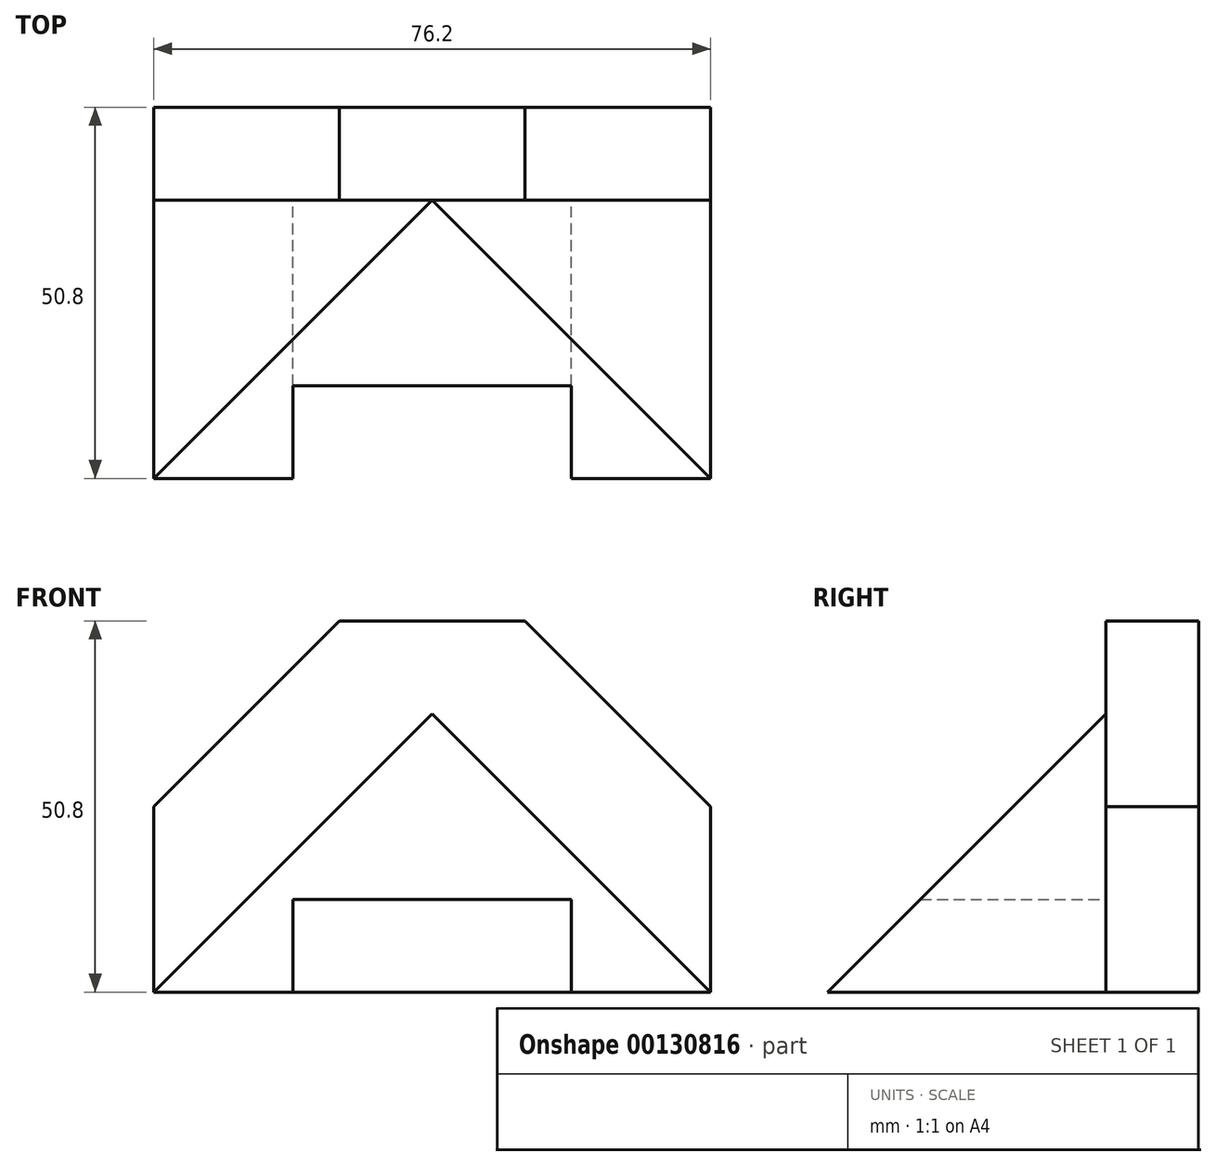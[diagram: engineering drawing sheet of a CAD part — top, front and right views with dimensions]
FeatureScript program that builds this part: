
annotation { "Feature Type Name" : "Feature", "Feature Type Description" : "" }
export const myFeature = defineFeature(function(context is Context, id is Id, definition is map)
    precondition{}
    {
        {
            var Q0;
            Q0=qCreatedBy(makeId("Top.planeOp"),FACE);
            var sketch = newSketch(context, id + "F0", { "sketchPlane" : qUnion([Q0])});
            skLineSegment(sketch, "E0", {"start": v(0, 0) * mm, "end": v(0, 50.8) * mm});
            skLineSegment(sketch, "E1", {"start": v(0, 50.8) * mm, "end": v(76.2, 50.8) * mm});
            skLineSegment(sketch, "E2", {"start": v(76.2, 50.8) * mm, "end": v(76.2, 0) * mm});
            skLineSegment(sketch, "E3", {"start": v(76.2, 0) * mm, "end": v(57.15, 0) * mm});
            skLineSegment(sketch, "E4", {"start": v(57.15, 0) * mm, "end": v(57.15, 12.7) * mm});
            skLineSegment(sketch, "E5", {"start": v(57.15, 12.7) * mm, "end": v(19.05, 12.7) * mm});
            skLineSegment(sketch, "E6", {"start": v(19.05, 12.7) * mm, "end": v(19.05, 0) * mm});
            skLineSegment(sketch, "E7", {"start": v(19.05, 0) * mm, "end": v(0, 0) * mm});
            skLineSegment(sketch, "E8", {"start": v(0, 38.1) * mm, "end": v(76.2, 38.1) * mm});
            skLineSegment(sketch, "E9", {"start": v(38.1, 38.1) * mm, "end": v(0, 0) * mm});
            skLineSegment(sketch, "E10", {"start": v(38.1, 38.1) * mm, "end": v(76.2, 0) * mm});
            skLineSegment(sketch, "E11", {"start": v(25.4, 38.1) * mm, "end": v(25.4, 50.8) * mm});
            skLineSegment(sketch, "E12", {"start": v(50.8, 50.8) * mm, "end": v(50.8, 38.1) * mm});
            skSolve(sketch);
        }
        {
            var Q0;
            {var subQ5=sQuery(id+"F0.wireOp",EDGE,"E11");Q0=makeQuery(id+"F0.imprint","IMPRINT",FACE,{"disambiguationData":[TD([[makeQuery(id+"F0.imprint","IMPRINT",EDGE,{"derivedFrom":subQ5}),1.0]])]});}
            var Q1;
            {var subQ3=sQuery(id+"F0.wireOp",EDGE,"E11");Q1=makeQuery(id+"F0.imprint","IMPRINT",FACE,{"disambiguationData":[TD([[makeQuery(id+"F0.imprint","IMPRINT",EDGE,{"derivedFrom":subQ3}),-1.0]])]});}
            var Q2;
            {var subQ3=sQuery(id+"F0.wireOp",EDGE,"E12");Q2=makeQuery(id+"F0.imprint","IMPRINT",FACE,{"disambiguationData":[TD([[makeQuery(id+"F0.imprint","IMPRINT",EDGE,{"derivedFrom":subQ3}),1.0]])]});}
            extrude(context, id + "F1", {"entities" : qUnion([Q0, Q1, Q2]), "depth" : 50.8 * mm});
        }
        {
            var Q0;
            Q0=makeQuery(id+"F1.opExtrude","SWEPT_FACE",FACE,{"disambiguationData":[OSD([sQuery(id+"F0.wireOp",EDGE,"E1")])]});
            var sketch = newSketch(context, id + "F2", { "sketchPlane" : qUnion([Q0])});
            skLineSegment(sketch, "E13", {"start": v(0, 25.4) * mm, "end": v(-25.4, 50.8) * mm});
            skLineSegment(sketch, "E14", {"start": v(-76.2, 25.4) * mm, "end": v(-50.8, 50.8) * mm});
            skSolve(sketch);
        }
        {
            var Q0;
            {var subQ0=sQuery(id+"F2.wireOp",EDGE,"E14");Q0=makeQuery(id+"F2.imprint","IMPRINT",FACE,{"disambiguationData":[TD([[makeQuery(id+"F2.imprint","IMPRINT",EDGE,{"derivedFrom":subQ0}),1.0]])]});}
            var Q1;
            {var subQ0=sQuery(id+"F2.wireOp",EDGE,"E13");Q1=makeQuery(id+"F2.imprint","IMPRINT",FACE,{"disambiguationData":[TD([[makeQuery(id+"F2.imprint","IMPRINT",EDGE,{"derivedFrom":subQ0}),-1.0]])]});}
            extrude(context, id + "F3", {"entities" : qUnion([Q0, Q1]), "operationType" : NewBodyOperationType.REMOVE, "oppositeDirection" : true, "depth" : 12.7 * mm});
        }
        {
            var Q0;
            Q0=makeQuery(id+"F1.opExtrude","SWEPT_FACE",FACE,{"disambiguationData":[OSD([sQuery(id+"F0.wireOp",EDGE,"E8")])]});
            var sketch = newSketch(context, id + "F4", { "sketchPlane" : qUnion([Q0])});
            skLineSegment(sketch, "E15", {"start": v(0, 0) * mm, "end": v(38.1, 38.1) * mm});
            skPoint(sketch, "E15.endSnap0", {"position": v(38.1, 50.8) * mm});
            skLineSegment(sketch, "E16", {"start": v(38.1, 38.1) * mm, "end": v(76.2, 0) * mm});
            skLineSegment(sketch, "E17", {"start": v(76.2, 0) * mm, "end": v(57.15, 0) * mm});
            skLineSegment(sketch, "E18", {"start": v(57.15, 0) * mm, "end": v(57.15, 12.7) * mm});
            skLineSegment(sketch, "E19", {"start": v(57.15, 12.7) * mm, "end": v(19.05, 12.7) * mm});
            skLineSegment(sketch, "E20", {"start": v(19.05, 12.7) * mm, "end": v(19.05, 0) * mm});
            skLineSegment(sketch, "E21", {"start": v(19.05, 0) * mm, "end": v(0, 0) * mm});
            skSolve(sketch);
        }
        {
            var Q0;
            Q0=makeQuery(id+"F4.imprint","IMPRINT",FACE,{"disambiguationData":[TD([[makeQuery(id+"F4.imprint","IMPRINT",EDGE,{"derivedFrom":sQuery(id+"F4.wireOp",EDGE,"E15")}),-1.0]])]});
            extrude(context, id + "F5", {"entities" : qUnion([Q0]), "operationType" : NewBodyOperationType.ADD, "depth" : 38.1 * mm});
        }
        {
            var Q0;
            Q0=makeQuery(id+"F1.opExtrude","SWEPT_FACE",FACE,{"disambiguationData":[OSD([sQuery(id+"F0.wireOp",EDGE,"E2")])]});
            var sketch = newSketch(context, id + "F6", { "sketchPlane" : qUnion([Q0])});
            skLineSegment(sketch, "E22.0", {"start": v(0, 38.1) * mm, "end": v(38.1, 38.1) * mm});
            skLineSegment(sketch, "E23", {"start": v(38.1, 38.1) * mm, "end": v(0, 0) * mm});
            skLineSegment(sketch, "E24", {"start": v(0, 0) * mm, "end": v(0, 38.1) * mm});
            skSolve(sketch);
        }
        {
            var Q0;
            Q0 = qSketchRegion(id + "F6", true);
            var Q1;
            Q1=makeQuery(id+"F6.imprint","IMPRINT",FACE,{"disambiguationData":[TD([[makeQuery(id+"F6.imprint","IMPRINT",EDGE,{"derivedFrom":sQuery(id+"F6.wireOp",EDGE,"E22.0")}),-1.0]])]});
            extrude(context, id + "F7", {"entities" : qUnion([Q0, Q1]), "operationType" : NewBodyOperationType.REMOVE, "endBound" : BoundingType.THROUGH_ALL, "oppositeDirection" : true, "depth" : 25.4 * mm});
        }
    });
